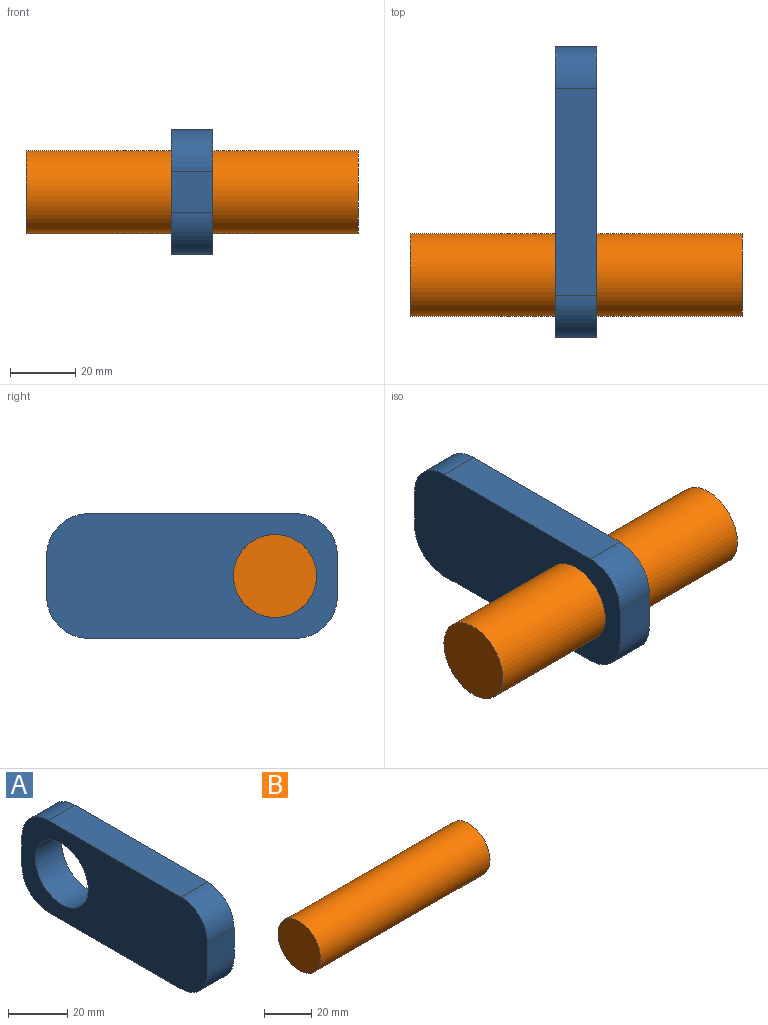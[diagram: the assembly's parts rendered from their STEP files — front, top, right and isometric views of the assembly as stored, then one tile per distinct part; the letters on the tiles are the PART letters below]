
ASSEMBLY  parts=2 mates=1
PART A: 11 faces, bbox 12.7x88.9x38.1 mm
  f0: plane 12.7x12.7mm, normal (0,1,0), area 161.3mm2, adj f5,f6,f7,f10
  f1: plane 63.5x12.7mm, normal (0,0,1), area 806.5mm2, adj f5,f6,f7,f8
  f2: plane 12.7x12.7mm, normal (0,-1,0), area 161.3mm2, adj f5,f6,f8,f9
  f3: plane 63.5x12.7mm, normal (0,0,-1), area 806.5mm2, adj f5,f6,f9,f10
  f4: cylinder r=12.7mm len=25.4mm, axis (-1,0,0), area 1013.4mm2, adj f5,f6
  f5: plane 88.9x38.1mm, normal (1,0,0), area 2741.9mm2, adj f0,f1,f2,f3,f4,f7,f8,f9
  f6: plane 88.9x38.1mm, normal (-1,0,0), area 2741.9mm2, adj f0,f1,f2,f3,f4,f7,f8,f9
  f7: cylinder r=12.7mm len=12.7mm, axis (1,0,0), area 253.4mm2, adj f0,f1,f5,f6
  f8: cylinder r=12.7mm len=12.7mm, axis (-1,0,0), area 253.4mm2, adj f1,f2,f5,f6
  f9: cylinder r=12.7mm len=12.7mm, axis (1,0,0), area 253.4mm2, adj f2,f3,f5,f6
  f10: cylinder r=12.7mm len=12.7mm, axis (-1,0,0), area 253.4mm2, adj f0,f3,f5,f6
PART B: 3 faces, bbox 101.6x25.4x25.4 mm
  f0: cylinder r=12.7mm len=101.6mm, axis (-1,0,0), area 8107.3mm2, adj f1,f2
  f1: plane 25.4x25.4mm, normal (1,0,0), area 506.7mm2, adj f0
  f2: plane 25.4x25.4mm, normal (-1,0,0), area 506.7mm2, adj f0
PLACE A rot(axis=(1,0,0),180deg) t=(0,0,0)mm
PLACE B at identity fixed
MATE revolute B.f0 <-> A.f4  axis (-1,0,0) through (0,0,0)mm
